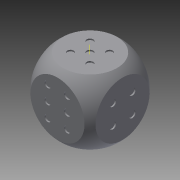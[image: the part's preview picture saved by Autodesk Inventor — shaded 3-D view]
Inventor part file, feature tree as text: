
AUTODESK INVENTOR PART (.ipt)
format: ipt  version: 2015 SP2 (Build 190223200, 223)  size: 212,992 bytes
history: native  units: mm
features: sketch x8, extrude x7, other x7, revolve x1, plane x1, pattern_linear x1, pattern_circular x1
ambient origin geometry x8: Origin, YZ Plane, XZ Plane, XY Plane, X Axis, Y Axis, Z Axis, Center Point
bodies: Volumenkörper1 (feature_tree), Volumenkörper2 (feature_tree), Volumenkörper3 (feature_tree), Volumenkörper4 (feature_tree), Volumenkörper5 (feature_tree), Volumenkörper6 (feature_tree), Volumenkörper7 (feature_tree), Volumenkörper8 (feature_tree)
feature tree (26):
  revolve  "Umdrehung1"
  extrude  "Extrusion1"  Depth=5.0mm
  other  "Kombinieren1"
  plane  "Arbeitsebene1"
  extrude  "Extrusion2"  Depth=3.25mm
  other  "Kombinieren2"
  extrude  "Extrusion3"  TaperAngle=360.0deg  [1 undecoded]
  pattern_linear  "Rechteckige Anordnung1"  Spacing1=1.25mm  [1 undecoded]
  other  "Kombinieren3"
  extrude  "Extrusion4"  Depth=0.1mm TaperAngle=0.0deg
  pattern_circular  "Runde Anordnung1"  Count=2  [1 undecoded]
  other  "Kombinieren4"
  extrude  "Extrusion5"  Depth=0.1mm
  other  "Kombinieren5"
  extrude  "Extrusion7"  Depth=0.1mm
  other  "Kombinieren6"
  extrude  "Extrusion8"  Depth=0.1mm
  other  "Kombinieren7"
  sketch  "Skizze1"  dims[d0=5.0mm d1=5.0mm]
  sketch  "Skizze3"  dims[d2=5.0mm d3=0.0mm d6=3.25mm]
  sketch  "Skizze5"  dims[d7=180.0deg d8=360.0deg]
  sketch  "Skizze6"  dims[d14=0.1mm]
  sketch  "Skizze7"  dims[d19=0.5mm]
  sketch  "Skizze8"  dims[d20=0.2mm d21=0.0mm]
  sketch  "Skizze9"  dims[d22=0.5mm]
  sketch  "Skizze10"  dims[d23=0.75mm d24=1.25mm d25=0.1mm d26=0.0mm d27=20.0mm d29=1.5mm d30=30.0mm d32=2.25mm d33=0.5mm d35=0.75mm d36=0.75mm d37=0.1mm d38=0.0mm d39=40.0mm d40=360.0deg d43=0.5mm d44=0.1mm d45=0.0mm d46=0.5mm d49=0.5mm d50=0.1mm d51=0.0mm d52=0.5mm d53=0.5mm d54=40.0mm d56=360.0deg d58=0.1mm d59=0.0mm]
note: 3 required parameter values undecoded (feature->parameter linkage not recoverable at this tier; creation-order binding heuristic only, values carry confidence <= 0.55)
